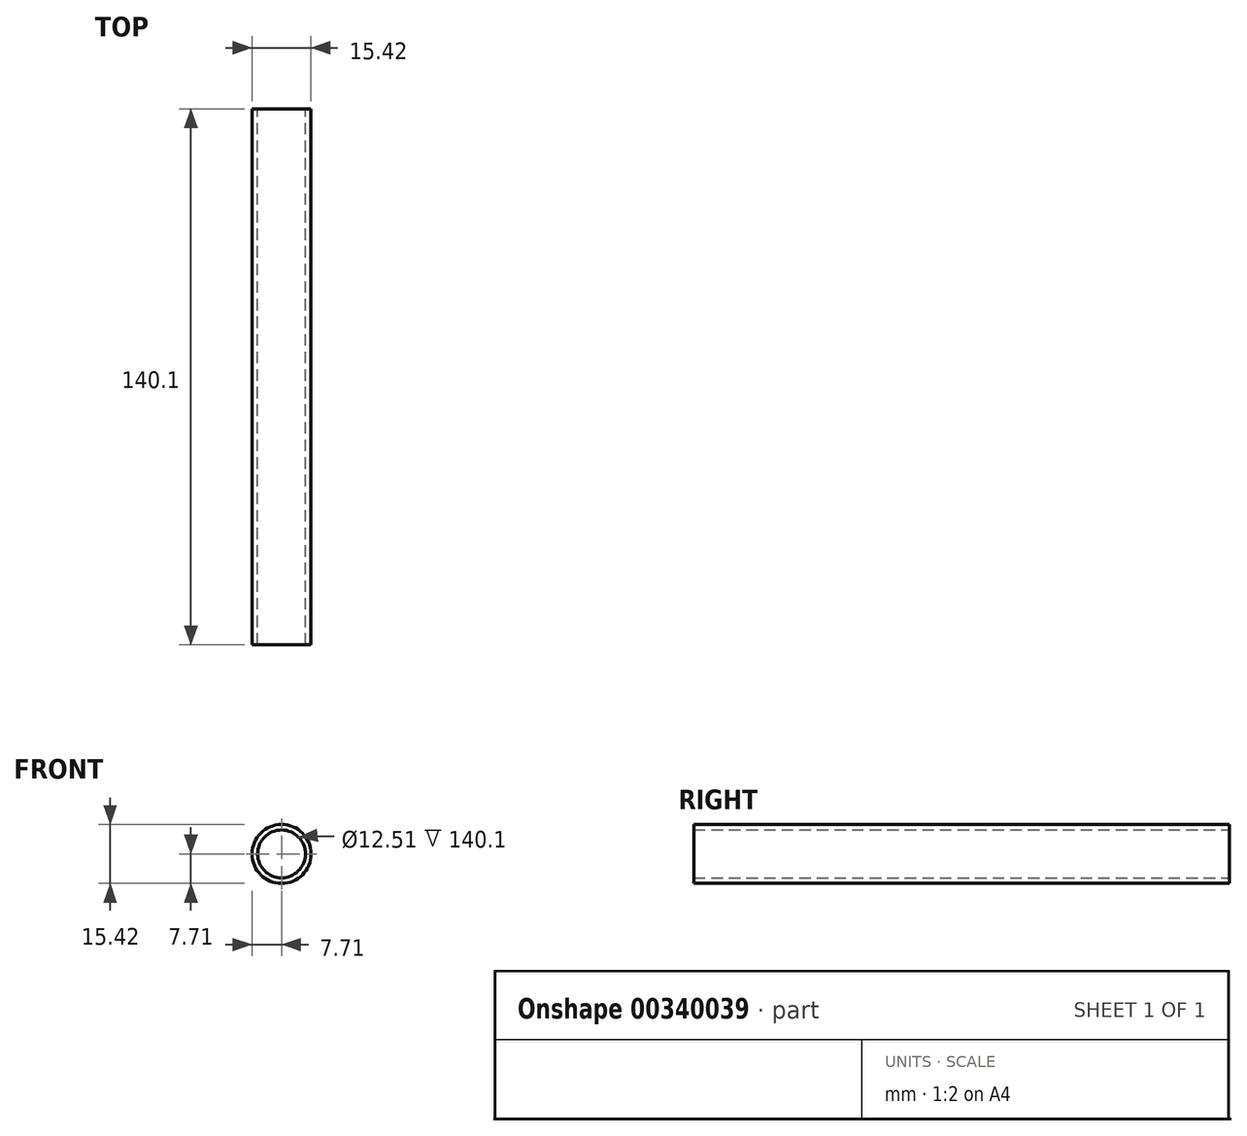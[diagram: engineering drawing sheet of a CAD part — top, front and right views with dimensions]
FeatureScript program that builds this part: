
annotation { "Feature Type Name" : "Feature", "Feature Type Description" : "" }
export const myFeature = defineFeature(function(context is Context, id is Id, definition is map)
    precondition{}
    {
        {
            var Q0;
            Q0=qCreatedBy(makeId("Front.planeOp"),FACE);
            var sketch = newSketch(context, id + "F0", { "sketchPlane" : qUnion([Q0])});
            skCircle(sketch, "E0", {"center": v(0, 0) * mm, "radius": 7.71 * mm});
            skCircle(sketch, "E1", {"center": v(0, 0) * mm, "radius": 6.26 * mm});
            skSolve(sketch);
        }
        {
            var Q0;
            Q0 = qSketchRegion(id + "F0", true);
            extrude(context, id + "F1", {"entities" : qUnion([Q0]), "depth" : 140.1 * mm});
        }
    });
